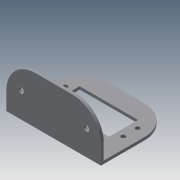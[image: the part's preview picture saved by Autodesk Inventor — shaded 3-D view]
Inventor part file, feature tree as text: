
AUTODESK INVENTOR PART (.ipt)
format: ipt  version: 2013 (Build 170138000, 138)  size: 136,192 bytes
history: native  units: mm
features: extrude x5, sketch x5, fillet x2
ambient origin geometry x8: Origin, YZ Plane, XZ Plane, XY Plane, X Axis, Y Axis, Z Axis, Center Point
bodies: Solid1 (feature_tree)
feature tree (12):
  extrude  "Extrusion1"  Depth=50.0mm
  extrude  "Extrusion2"  Depth=2.0mm
  extrude  "Extrusion3"  Depth=28.0mm
  extrude  "Extrusion4"  Depth=20.0mm
  fillet  "Fillet1"  Radius=3.0mm
  fillet  "Fillet2"  Radius=3.0mm
  extrude  "Extrusion5"  Depth=3.0mm
  sketch  "Sketch1"  dims[d0=65.0mm d1=50.0mm]
  sketch  "Sketch2"  dims[d2=2.0mm d3=0.0mm d4=2.0mm]
  sketch  "Sketch3"  dims[d5=48.0mm d6=0.0mm d10=28.0mm]
  sketch  "Sketch4"  dims[d11=40.2mm d12=20.0mm d15=3.0mm d16=3.0mm]
  sketch  "Sketch5"  dims[d18=3.0mm d20=3.0mm d21=2.0mm d22=0.0mm d23=17.4mm d24=0.0mm d25=20.0mm d26=20.0mm d29=4.0mm d32=4.0mm d33=2.0mm d34=0.0mm]
